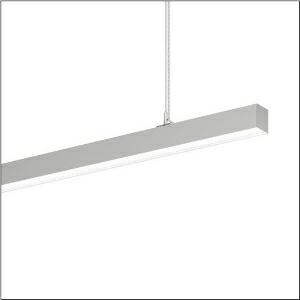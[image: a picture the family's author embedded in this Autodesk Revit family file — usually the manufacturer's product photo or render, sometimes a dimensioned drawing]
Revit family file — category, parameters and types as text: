
# Revit family: silica_21_51mx33db49sb
name_source: partatom
category: Lighting Fixtures
units: mm (PartAtom-declared; Revit-internal decimal feet)

## family parameters
Cut with Voids When Loaded = No
Host = Face
Light Source = No
Part Type = Normal
Room Calculation Point = No
Round Connector Dimension = Use Diameter
Shared = No

## types (1)
- --- (1 x LED, 7390 lm, 48.3 W, 4000K)
    Apparent Load = 48 VA
    CIE Flux Codes = 78 96 99 55 100
    Color Rendering = 80
    Color Temperature = 4000K
    Default Elevation = 1800 mm
    Description = Silica 21, office luminaire, primary optical cover: prismatic diffuser, of PMMA, CAT 2 (L<= 3000cd/m²), light emission: direct/indirect distribution, primary light characteristic: symmetric, installation type: suspended mounting, LED, rated luminous flux: 7.390lm, luminous efficacy: 153lm/W, light colour: 840, colour temperature: 4000K, control gear: DALI 2, with terminal, 3+2-pole, max. 2.5mm², mains connection: 220..240V, AC, 50/60Hz, rated input power: 48.3W, luminaire housing, of aluminium, metallic grey (RAL 9006), length: 1.504mm, width: 53mm, height: 53mm, protection rating (complete): IP20, insulation class (complete): insulation class I (protective earthing), certification: CE, permissible operating ambient temperature: 0..+35°C, standard: EN 50419, packaging unit: 1 piece
    Height = 53 mm
    Lamp = 1 x LED
    Lamp Light Flux = 7390 lm
    Lamp Power = 48.3 W
    Lamp count = 1
    Length = 1504 mm
    Luminous efficacy = 153 lm/W
    Manufacturer = Siteco
    ModVariant = No
    Model = 51MX33DB49SB
    Mounting Place = Ceiling
    Mounting Type = Pendant
    Number of Poles = 1
    OnlyDefault = Yes
    Power Factor = 1
    Product Name = Silica 21
    Product group = office luminaire | ceiling pendant
    ProductGroupID = 903
    Protection Class = Protection class I
    Protection Degree = IP 20
    RLX_Detail_Level = 1
    RLX_Emergency_Light_Flux = 0 lm
    RLX_Emergency_Type = 0
    RLX_Emergency_Type_DB = No
    RlxData = <blob elided: 23521 chars, md5=b2774898>
    Socket = socket
    Standby Power = 0 W
    System Light Flux = 7390 lm
    System Power = 48 W
    Type Comments = factory setting: luminous flux: 100 % | dim-lin: 254 | 323 mA
    Type Image = l_1335864.jpg
    URL = http://relux.com
    VarID = @adj_118503
    Voltage = 0 V
    Weight = 0.00 kg
    Width = 53 mm

## geometry (parser evidence)
native form markers: Blend x4, Sweep x12
no freeform markers — native parametric forms only
